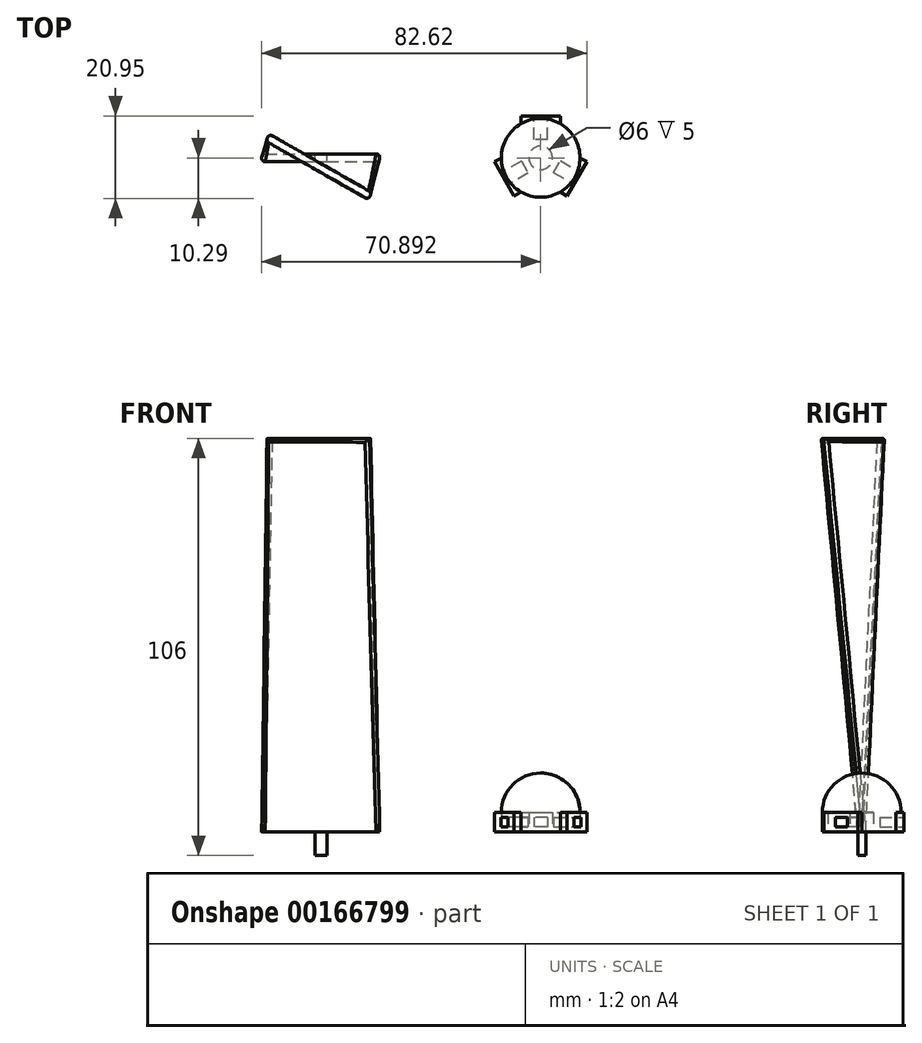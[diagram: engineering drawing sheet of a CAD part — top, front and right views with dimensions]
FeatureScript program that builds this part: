
annotation { "Feature Type Name" : "Feature", "Feature Type Description" : "" }
export const myFeature = defineFeature(function(context is Context, id is Id, definition is map)
    precondition{}
    {
        {
            var Q0;
            Q0=qCreatedBy(makeId("Top.planeOp"),FACE);
            var sketch = newSketch(context, id + "F0", { "sketchPlane" : qUnion([Q0])});
            skLineSegment(sketch, "E0.bottom", {"start": v(-43.93, 1) * mm, "end": v(-13.93, 1) * mm});
            skLineSegment(sketch, "E0.top", {"start": v(-43.93, -1) * mm, "end": v(-13.93, -1) * mm});
            skLineSegment(sketch, "E0.left", {"start": v(-43.93, 1) * mm, "end": v(-43.93, -1) * mm});
            skLineSegment(sketch, "E0.right", {"start": v(-13.93, 1) * mm, "end": v(-13.93, -1) * mm});
            skSolve(sketch);
        }
        {
            var Q0;
            Q0=makeQuery(id+"F0.imprint","IMPRINT",FACE,{"disambiguationData":[TD([[makeQuery(id+"F0.imprint","IMPRINT",EDGE,{"derivedFrom":sQuery(id+"F0.wireOp",EDGE,"E0.bottom")}),-1.0]])]});
            cPlane(context, id + "F1", {"entities" : qUnion([Q0]), "cplaneType" : CPlaneType.OFFSET, "offset" : 100 * mm, "width" : 150 * mm, "height" : 150 * mm});
        }
        {
            var Q0;
            Q0=qCreatedBy(id+"F1.planeOp",FACE);
            var sketch = newSketch(context, id + "F2", { "sketchPlane" : qUnion([Q0])});
            skLineSegment(sketch, "E1", {"start": v(-41.92, 6.07) * mm, "end": v(-15.93, -8.93) * mm});
            skLineSegment(sketch, "E2", {"start": v(-15.93, -8.93) * mm, "end": v(-16.93, -10.66) * mm});
            skLineSegment(sketch, "E3", {"start": v(-16.93, -10.66) * mm, "end": v(-42.92, 4.34) * mm});
            skLineSegment(sketch, "E4", {"start": v(-42.92, 4.34) * mm, "end": v(-41.92, 6.07) * mm});
            skLineSegment(sketch, "E5.0", {"start": v(-43.93, 1) * mm, "end": v(-43.93, -1) * mm, "construction": true});
            skLineSegment(sketch, "E6.0", {"start": v(-43.93, 1) * mm, "end": v(-13.93, 1) * mm, "construction": true});
            skPoint(sketch, "E7", {"position": v(-28.93, 1) * mm});
            skPoint(sketch, "E8", {"position": v(-28.93, -1.43) * mm});
            skLineSegment(sketch, "E9", {"start": v(-28.93, 1) * mm, "end": v(-28.93, -1.43) * mm, "construction": true});
            skSolve(sketch);
        }
        {
            var Q0;
            Q0=makeQuery(id+"F0.imprint","IMPRINT",FACE,{"disambiguationData":[TD([[makeQuery(id+"F0.imprint","IMPRINT",EDGE,{"derivedFrom":sQuery(id+"F0.wireOp",EDGE,"E0.bottom")}),-1.0]])]});
            var Q1;
            Q1=makeQuery(id+"F2.imprint","IMPRINT",FACE,{"disambiguationData":[TD([[makeQuery(id+"F2.imprint","IMPRINT",EDGE,{"derivedFrom":sQuery(id+"F2.wireOp",EDGE,"E1")}),-1.0]])]});
            loft(context, id + "F3", {"sheetProfilesArray" : [{ "sheetProfileEntities" : qUnion([Q0]) }, { "sheetProfileEntities" : qUnion([Q1]) }]});
        }
        {
            var Q0;
            Q0=makeQuery(id+"F3.opLoft","SWEPT_EDGE",EDGE,{"disambiguationData":[OSD([sQuery(id+"F0.wireOp",EDGE,"E0.bottom"),sQuery(id+"F0.wireOp",EDGE,"E0.left"),sQuery(id+"F2.wireOp",EDGE,"E1"),sQuery(id+"F2.wireOp",EDGE,"E4")])]});
            var Q1;
            Q1=makeQuery(id+"F3.opLoft","SWEPT_EDGE",EDGE,{"disambiguationData":[OSD([sQuery(id+"F0.wireOp",EDGE,"E0.top"),sQuery(id+"F0.wireOp",EDGE,"E0.left"),sQuery(id+"F2.wireOp",EDGE,"E3"),sQuery(id+"F2.wireOp",EDGE,"E4")])]});
            var Q2;
            Q2=makeQuery(id+"F3.opLoft","SWEPT_EDGE",EDGE,{"disambiguationData":[OSD([sQuery(id+"F0.wireOp",EDGE,"E0.bottom"),sQuery(id+"F0.wireOp",EDGE,"E0.right"),sQuery(id+"F2.wireOp",EDGE,"E1"),sQuery(id+"F2.wireOp",EDGE,"E2")])]});
            var Q3;
            Q3=makeQuery(id+"F3.opLoft","SWEPT_EDGE",EDGE,{"disambiguationData":[OSD([sQuery(id+"F0.wireOp",EDGE,"E0.top"),sQuery(id+"F0.wireOp",EDGE,"E0.right"),sQuery(id+"F2.wireOp",EDGE,"E2"),sQuery(id+"F2.wireOp",EDGE,"E3")])]});
            var Q4;
            Q4=makeQuery(id+"F3.opLoft","MID_CAP_EDGE",EDGE,{"disambiguationData":[OSD([sQuery(id+"F2.wireOp",EDGE,"E1"),sQuery(id+"F2.wireOp",EDGE,"E2"),sQuery(id+"F2.wireOp",EDGE,"E4")])],"capPos":1.0});
            var Q5;
            Q5=makeQuery(id+"F3.opLoft","MID_CAP_EDGE",EDGE,{"disambiguationData":[OSD([sQuery(id+"F2.wireOp",EDGE,"E2"),sQuery(id+"F2.wireOp",EDGE,"E3"),sQuery(id+"F2.wireOp",EDGE,"E4")])],"capPos":1.0});
            fillet(context, id + "F4", {"entities" : qUnion([Q0, Q1, Q2, Q3, Q4, Q5]), "radius" : 0.9 * mm, "tangentPropagation" : true, "allowEdgeOverflow" : false});
        }
        {
            var Q0;
            Q0=makeQuery(id+"F3.opLoft","CAP_FACE",FACE,{"disambiguationData":[OSD([makeQuery(id+"F0.imprint","IMPRINT",FACE,{"disambiguationData":[TD([[makeQuery(id+"F0.imprint","IMPRINT",EDGE,{"derivedFrom":sQuery(id+"F0.wireOp",EDGE,"E0.bottom")}),-1.0]])]})])],"isStart":true});
            var sketch = newSketch(context, id + "F5", { "sketchPlane" : qUnion([Q0])});
            skLineSegment(sketch, "E10", {"start": v(-28.93, 1) * mm, "end": v(-28.93, -1) * mm});
            skLineSegment(sketch, "E11.bottom", {"start": v(-30.33, 1) * mm, "end": v(-27.33, 1) * mm});
            skLineSegment(sketch, "E11.top", {"start": v(-30.33, -1) * mm, "end": v(-27.33, -1) * mm});
            skLineSegment(sketch, "E11.left", {"start": v(-30.33, 1) * mm, "end": v(-30.33, -1) * mm});
            skLineSegment(sketch, "E11.right", {"start": v(-27.33, 1) * mm, "end": v(-27.33, -1) * mm});
            skSolve(sketch);
        }
        {
            var Q0;
            {var subQ0=sQuery(id+"F5.wireOp",EDGE,"E10");Q0=makeQuery(id+"F5.imprint","IMPRINT",FACE,{"disambiguationData":[TD([[makeQuery(id+"F5.imprint","IMPRINT",EDGE,{"derivedFrom":subQ0}),1.0]])]});}
            var Q1;
            {var subQ0=sQuery(id+"F5.wireOp",EDGE,"E10");Q1=makeQuery(id+"F5.imprint","IMPRINT",FACE,{"disambiguationData":[TD([[makeQuery(id+"F5.imprint","IMPRINT",EDGE,{"derivedFrom":subQ0}),-1.0]])]});}
            extrude(context, id + "F6", {"entities" : qUnion([Q0, Q1]), "operationType" : NewBodyOperationType.ADD, "depth" : 6 * mm});
        }
        {
            var Q0;
            Q0=qCreatedBy(makeId("Top.planeOp"),FACE);
            var sketch = newSketch(context, id + "F7", { "sketchPlane" : qUnion([Q0])});
            skCircle(sketch, "E12", {"center": v(26.96, 0) * mm, "radius": 10 * mm});
            skSolve(sketch);
        }
        {
            var Q0;
            Q0=makeQuery(id+"F7.imprint","IMPRINT",FACE,{"disambiguationData":[TD([[makeQuery(id+"F7.imprint","IMPRINT",EDGE,{"derivedFrom":sQuery(id+"F7.wireOp",EDGE,"E12")}),1.0]])]});
            extrude(context, id + "F8", {"entities" : qUnion([Q0]), "depth" : 15 * mm});
        }
        {
            var Q0;
            Q0=makeQuery(id+"F8.opExtrude","CAP_EDGE",EDGE,{"disambiguationData":[OSD([sQuery(id+"F7.wireOp",EDGE,"E12")])],"isStart":false});
            fillet(context, id + "F9", {"entities" : qUnion([Q0]), "radius" : 10 * mm, "tangentPropagation" : true, "allowEdgeOverflow" : false});
        }
        {
            var Q0;
            Q0=qCreatedBy(makeId("Top.planeOp"),FACE);
            var sketch = newSketch(context, id + "F10", { "sketchPlane" : qUnion([Q0])});
            skCircle(sketch, "E13.0", {"center": v(26.96, 0) * mm, "radius": 10 * mm});
            skLineSegment(sketch, "E14", {"start": v(26.96, 0) * mm, "end": v(26.96, 18.07) * mm, "construction": true});
            skLineSegment(sketch, "E15", {"start": v(21.96, 8.66) * mm, "end": v(21.96, 10.66) * mm});
            skLineSegment(sketch, "E16", {"start": v(21.96, 10.66) * mm, "end": v(31.96, 10.66) * mm});
            skLineSegment(sketch, "E17", {"start": v(31.96, 10.66) * mm, "end": v(31.96, 8.66) * mm});
            skSolve(sketch);
        }
        {
            var Q0;
            {var subQ0=sQuery(id+"F10.wireOp",EDGE,"E15");Q0=makeQuery(id+"F10.imprint","IMPRINT",FACE,{"disambiguationData":[TD([[makeQuery(id+"F10.imprint","IMPRINT",EDGE,{"derivedFrom":subQ0}),-1.0]])]});}
            extrude(context, id + "F11", {"entities" : qUnion([Q0]), "operationType" : NewBodyOperationType.ADD, "depth" : 5 * mm});
        }
        {
            var Q0;
            Q0=makeQuery(id+"F11.opExtrude","SWEPT_FACE",FACE,{"disambiguationData":[OSD([sQuery(id+"F10.wireOp",EDGE,"E16")])]});
            var Q1;
            Q1=makeQuery(id+"F11.opExtrude","SWEPT_FACE",FACE,{"disambiguationData":[OSD([sQuery(id+"F10.wireOp",EDGE,"E15")])]});
            var Q2;
            Q2=makeQuery(id+"F11.opExtrude","CAP_FACE",FACE,{"disambiguationData":[OSD([sQuery(id+"F10.wireOp",EDGE,"E13.0"),sQuery(id+"F10.wireOp",EDGE,"E15"),sQuery(id+"F10.wireOp",EDGE,"E16"),sQuery(id+"F10.wireOp",EDGE,"E17")])],"isStart":false});
            var Q3;
            Q3=makeQuery(id+"F11.opExtrude","SWEPT_FACE",FACE,{"disambiguationData":[OSD([sQuery(id+"F10.wireOp",EDGE,"E17")])]});
            var Q4;
            Q4=makeQuery(id+"F8.opExtrude","SWEPT_FACE",FACE,{"disambiguationData":[OSD([sQuery(id+"F7.wireOp",EDGE,"E12")])]});
            circularPattern(context, id + "F12", {"patternType" : PatternType.FACE, "faces" : qUnion([Q0, Q1, Q2, Q3]), "axis" : qUnion([Q4]), "angle" : 120 * degree, "instanceCount" : 3});
        }
        {
            var Q0;
            Q0=makeQuery(id+"F11.opExtrude","SWEPT_FACE",FACE,{"disambiguationData":[OSD([sQuery(id+"F10.wireOp",EDGE,"E16")])]});
            var sketch = newSketch(context, id + "F13", { "sketchPlane" : qUnion([Q0])});
            skLineSegment(sketch, "E18.0.0", {"start": v(-31.96, 0) * mm, "end": v(-21.96, 0) * mm});
            skLineSegment(sketch, "E18.0.1", {"start": v(-21.96, 0) * mm, "end": v(-21.96, 5) * mm});
            skLineSegment(sketch, "E18.0.2", {"start": v(-21.96, 5) * mm, "end": v(-31.96, 5) * mm});
            skLineSegment(sketch, "E18.0.3", {"start": v(-31.96, 5) * mm, "end": v(-31.96, 0) * mm});
            skLineSegment(sketch, "E19.bottom", {"start": v(-28.71, 3.75) * mm, "end": v(-25.21, 3.75) * mm});
            skLineSegment(sketch, "E19.top", {"start": v(-28.71, 1.25) * mm, "end": v(-25.21, 1.25) * mm});
            skLineSegment(sketch, "E19.left", {"start": v(-28.71, 3.75) * mm, "end": v(-28.71, 1.25) * mm});
            skLineSegment(sketch, "E19.right", {"start": v(-25.21, 3.75) * mm, "end": v(-25.21, 1.25) * mm});
            skLineSegment(sketch, "E20", {"start": v(-26.96, 5) * mm, "end": v(-26.96, 0) * mm, "construction": true});
            skLineSegment(sketch, "E21", {"start": v(-31.96, 2.5) * mm, "end": v(-21.96, 2.5) * mm, "construction": true});
            skSolve(sketch);
        }
        {
            var Q0;
            Q0=makeQuery(id+"F13.imprint","IMPRINT",FACE,{"disambiguationData":[TD([[makeQuery(id+"F13.imprint","IMPRINT",EDGE,{"derivedFrom":sQuery(id+"F13.wireOp",EDGE,"E19.bottom")}),-1.0]])]});
            extrude(context, id + "F14", {"entities" : qUnion([Q0]), "operationType" : NewBodyOperationType.REMOVE, "oppositeDirection" : true, "depth" : 6 * mm});
        }
        {
            var Q0;
            Q0=makeQuery(id+"F12.opPattern","COPY",FACE,{"derivedFrom":makeQuery(id+"F11.opExtrude","SWEPT_FACE",FACE,{"disambiguationData":[OSD([sQuery(id+"F10.wireOp",EDGE,"E16")])]}),"instanceName":"1"});
            var sketch = newSketch(context, id + "F15", { "sketchPlane" : qUnion([Q0])});
            skLineSegment(sketch, "E22.0.0", {"start": v(8.48, 0) * mm, "end": v(18.48, 0) * mm});
            skLineSegment(sketch, "E22.0.1", {"start": v(18.48, 0) * mm, "end": v(18.48, 5) * mm});
            skLineSegment(sketch, "E22.0.2", {"start": v(18.48, 5) * mm, "end": v(8.48, 5) * mm});
            skLineSegment(sketch, "E22.0.3", {"start": v(8.48, 5) * mm, "end": v(8.48, 0) * mm});
            skLineSegment(sketch, "E23", {"start": v(13.48, 5) * mm, "end": v(13.48, 0) * mm, "construction": true});
            skLineSegment(sketch, "E24", {"start": v(8.48, 2.5) * mm, "end": v(18.48, 2.5) * mm, "construction": true});
            skLineSegment(sketch, "E25.bottom", {"start": v(11.9, 3.75) * mm, "end": v(15.4, 3.75) * mm});
            skLineSegment(sketch, "E25.top", {"start": v(11.9, 1.25) * mm, "end": v(15.4, 1.25) * mm});
            skLineSegment(sketch, "E25.left", {"start": v(11.9, 3.75) * mm, "end": v(11.9, 1.25) * mm});
            skLineSegment(sketch, "E25.right", {"start": v(15.4, 3.75) * mm, "end": v(15.4, 1.25) * mm});
            skSolve(sketch);
        }
        {
            var Q0;
            Q0=makeQuery(id+"F15.imprint","IMPRINT",FACE,{"disambiguationData":[TD([[makeQuery(id+"F15.imprint","IMPRINT",EDGE,{"derivedFrom":sQuery(id+"F15.wireOp",EDGE,"E25.bottom")}),-1.0]])]});
            extrude(context, id + "F16", {"entities" : qUnion([Q0]), "operationType" : NewBodyOperationType.REMOVE, "oppositeDirection" : true, "depth" : 6 * mm});
        }
        {
            var Q0;
            Q0=makeQuery(id+"F12.opPattern","COPY",FACE,{"derivedFrom":makeQuery(id+"F11.opExtrude","SWEPT_FACE",FACE,{"disambiguationData":[OSD([sQuery(id+"F10.wireOp",EDGE,"E16")])]}),"instanceName":"2"});
            var sketch = newSketch(context, id + "F17", { "sketchPlane" : qUnion([Q0])});
            skLineSegment(sketch, "E26.0.0", {"start": v(8.48, 0) * mm, "end": v(18.48, 0) * mm});
            skLineSegment(sketch, "E26.0.1", {"start": v(18.48, 0) * mm, "end": v(18.48, 5) * mm});
            skLineSegment(sketch, "E26.0.2", {"start": v(18.48, 5) * mm, "end": v(8.48, 5) * mm});
            skLineSegment(sketch, "E26.0.3", {"start": v(8.48, 5) * mm, "end": v(8.48, 0) * mm});
            skLineSegment(sketch, "E27", {"start": v(13.48, 5) * mm, "end": v(13.48, 0) * mm, "construction": true});
            skLineSegment(sketch, "E28", {"start": v(8.48, 2.5) * mm, "end": v(18.48, 2.5) * mm, "construction": true});
            skLineSegment(sketch, "E29.bottom", {"start": v(11.73, 3.75) * mm, "end": v(15.23, 3.75) * mm});
            skLineSegment(sketch, "E29.top", {"start": v(11.73, 1.25) * mm, "end": v(15.23, 1.25) * mm});
            skLineSegment(sketch, "E29.left", {"start": v(11.73, 3.75) * mm, "end": v(11.73, 1.25) * mm});
            skLineSegment(sketch, "E29.right", {"start": v(15.23, 3.75) * mm, "end": v(15.23, 1.25) * mm});
            skSolve(sketch);
        }
        {
            var Q0;
            Q0=makeQuery(id+"F17.imprint","IMPRINT",FACE,{"disambiguationData":[TD([[makeQuery(id+"F17.imprint","IMPRINT",EDGE,{"derivedFrom":sQuery(id+"F17.wireOp",EDGE,"E29.bottom")}),-1.0]])]});
            extrude(context, id + "F18", {"entities" : qUnion([Q0]), "operationType" : NewBodyOperationType.REMOVE, "oppositeDirection" : true, "depth" : 6 * mm});
        }
        {
            var Q0;
            Q0=makeQuery(id+"F11.boolean.opBoolean","MERGE",FACE,{"derivedFrom":[makeQuery(id+"F8.opExtrude","CAP_FACE",FACE,{"disambiguationData":[OSD([sQuery(id+"F7.wireOp",EDGE,"E12")])],"isStart":true}),makeQuery(id+"F11.opExtrude","CAP_FACE",FACE,{"disambiguationData":[OSD([sQuery(id+"F10.wireOp",EDGE,"E13.0"),sQuery(id+"F10.wireOp",EDGE,"E15"),sQuery(id+"F10.wireOp",EDGE,"E16"),sQuery(id+"F10.wireOp",EDGE,"E17")])],"isStart":true})]});
            var sketch = newSketch(context, id + "F19", { "sketchPlane" : qUnion([Q0])});
            skArc(sketch, "E30.0.0", {"start": v(16.96, 0) * mm, "mid": v(18.3, -5) * mm, "end": v(21.96, -8.66) * mm});
            skLineSegment(sketch, "E30.0.1", {"start": v(21.96, -8.66) * mm, "end": v(21.96, -10.66) * mm});
            skLineSegment(sketch, "E30.0.2", {"start": v(21.96, -10.66) * mm, "end": v(31.96, -10.66) * mm});
            skLineSegment(sketch, "E30.0.3", {"start": v(31.96, -10.66) * mm, "end": v(31.96, -8.66) * mm});
            skArc(sketch, "E30.0.4", {"start": v(31.96, -8.66) * mm, "mid": v(35.62, -5) * mm, "end": v(36.96, 0) * mm});
            skLineSegment(sketch, "E30.0.5", {"start": v(36.96, 0) * mm, "end": v(38.7, 1) * mm});
            skLineSegment(sketch, "E30.0.6", {"start": v(38.7, 1) * mm, "end": v(33.7, 9.66) * mm});
            skLineSegment(sketch, "E30.0.7", {"start": v(33.7, 9.66) * mm, "end": v(31.96, 8.66) * mm});
            skArc(sketch, "E30.0.8", {"start": v(31.96, 8.66) * mm, "mid": v(26.96, 10) * mm, "end": v(21.96, 8.66) * mm});
            skLineSegment(sketch, "E30.0.9", {"start": v(21.96, 8.66) * mm, "end": v(20.23, 9.66) * mm});
            skLineSegment(sketch, "E30.0.10", {"start": v(20.23, 9.66) * mm, "end": v(15.23, 1) * mm});
            skLineSegment(sketch, "E30.0.11", {"start": v(15.23, 1) * mm, "end": v(16.96, 0) * mm});
            skCircle(sketch, "E31", {"center": v(26.96, 0) * mm, "radius": 3 * mm});
            skSolve(sketch);
        }
        {
            var Q0;
            Q0=makeQuery(id+"F19.imprint","IMPRINT",FACE,{"disambiguationData":[TD([[makeQuery(id+"F19.imprint","IMPRINT",EDGE,{"derivedFrom":sQuery(id+"F19.wireOp",EDGE,"E31")}),1.0]])]});
            extrude(context, id + "F20", {"entities" : qUnion([Q0]), "operationType" : NewBodyOperationType.REMOVE, "oppositeDirection" : true, "depth" : 5 * mm});
        }
    });
